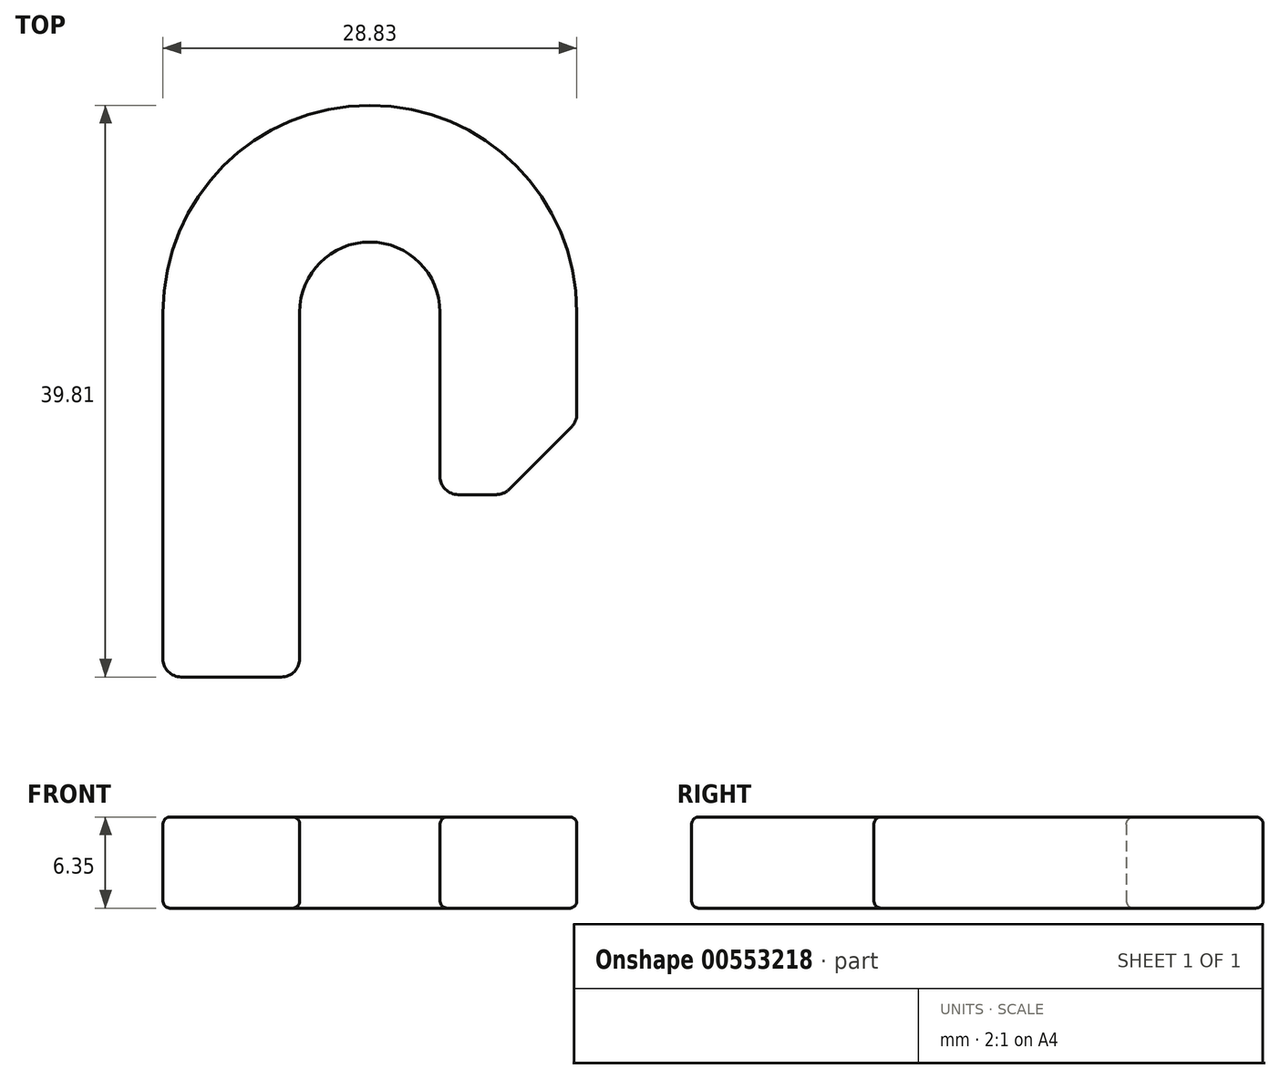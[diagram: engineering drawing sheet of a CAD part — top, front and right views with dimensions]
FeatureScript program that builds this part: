
annotation { "Feature Type Name" : "Feature", "Feature Type Description" : "" }
export const myFeature = defineFeature(function(context is Context, id is Id, definition is map)
    precondition{}
    {
        {
            var Q0;
            Q0=qCreatedBy(makeId("Top.planeOp"),FACE);
            var sketch = newSketch(context, id + "F0", { "sketchPlane" : qUnion([Q0])});
            skLineSegment(sketch, "E0", {"start": v(0, 0) * mm, "end": v(9.53, 0) * mm});
            skLineSegment(sketch, "E1", {"start": v(9.53, 0) * mm, "end": v(9.53, 25.4) * mm});
            skLineSegment(sketch, "E2", {"start": v(9.53, 25.4) * mm, "end": v(19.3, 25.4) * mm, "construction": true});
            skLineSegment(sketch, "E3", {"start": v(19.3, 25.4) * mm, "end": v(19.3, 0) * mm});
            skLineSegment(sketch, "E4", {"start": v(19.3, 0) * mm, "end": v(28.83, 0) * mm});
            skLineSegment(sketch, "E5", {"start": v(28.83, 0) * mm, "end": v(28.83, 25.4) * mm});
            skArc(sketch, "E6", {"start": v(19.3, 25.4) * mm, "mid": v(14.41, 30.29) * mm, "end": v(9.52, 25.4) * mm});
            skLineSegment(sketch, "E7", {"start": v(0, 0) * mm, "end": v(0, 25.4) * mm});
            skArc(sketch, "E8.trimOffspring", {"start": v(28.83, 25.4) * mm, "mid": v(14.41, 39.81) * mm, "end": v(0, 25.4) * mm});
            skLineSegment(sketch, "E9", {"start": v(19.3, 12.7) * mm, "end": v(28.83, 12.7) * mm});
            skSolve(sketch);
        }
        {
            var Q0;
            Q0=makeQuery(id+"F0.imprint","IMPRINT",FACE,{"disambiguationData":[TD([[makeQuery(id+"F0.imprint","IMPRINT",EDGE,{"derivedFrom":sQuery(id+"F0.wireOp",EDGE,"E0")}),1.0]])]});
            extrude(context, id + "F1", {"entities" : qUnion([Q0]), "depth" : 6.35 * mm, "offsetDistance" : 25.4 * mm});
        }
        {
            var Q0;
            Q0=makeQuery(id+"F1.opExtrude","SWEPT_EDGE",EDGE,{"disambiguationData":[OSD([sQuery(id+"F0.wireOp",EDGE,"E5"),sQuery(id+"F0.wireOp",EDGE,"E9")])]});
            chamfer(context, id + "F2", {"entities" : qUnion([Q0]), "width" : 5.08 * mm, "tangentPropagation" : true});
        }
        {
            var Q0;
            {var subQ0=sQuery(id+"F0.wireOp",EDGE,"E9");Q0=makeQuery(id+"F2.opChamfer","BLEND_EDGE",EDGE,{"blendedFrom":[makeQuery(id+"F1.opExtrude","SWEPT_EDGE",EDGE,{"disambiguationData":[OSD([sQuery(id+"F0.wireOp",EDGE,"E5"),subQ0])]}),makeQuery(id+"F1.opExtrude","SWEPT_FACE",FACE,{"disambiguationData":[OSD([subQ0])]})],"blendedInto":[makeQuery(id+"F1.opExtrude","SWEPT_FACE",FACE,{"disambiguationData":[OSD([subQ0])]})]});}
            var Q1;
            {var subQ0=sQuery(id+"F0.wireOp",EDGE,"E5");Q1=makeQuery(id+"F2.opChamfer","BLEND_EDGE",EDGE,{"blendedFrom":[makeQuery(id+"F1.opExtrude","SWEPT_EDGE",EDGE,{"disambiguationData":[OSD([subQ0,sQuery(id+"F0.wireOp",EDGE,"E9")])]}),makeQuery(id+"F1.opExtrude","SWEPT_FACE",FACE,{"disambiguationData":[OSD([subQ0])]})],"blendedInto":[makeQuery(id+"F1.opExtrude","SWEPT_FACE",FACE,{"disambiguationData":[OSD([subQ0])]})]});}
            var Q2;
            Q2=makeQuery(id+"F1.opExtrude","SWEPT_EDGE",EDGE,{"disambiguationData":[OSD([sQuery(id+"F0.wireOp",EDGE,"E3"),sQuery(id+"F0.wireOp",EDGE,"E9")])]});
            var Q3;
            Q3=makeQuery(id+"F1.opExtrude","SWEPT_EDGE",EDGE,{"disambiguationData":[OSD([sQuery(id+"F0.wireOp",EDGE,"E0"),sQuery(id+"F0.wireOp",EDGE,"E7")])]});
            var Q4;
            Q4=makeQuery(id+"F1.opExtrude","SWEPT_EDGE",EDGE,{"disambiguationData":[OSD([sQuery(id+"F0.wireOp",EDGE,"E0"),sQuery(id+"F0.wireOp",EDGE,"E1")])]});
            fillet(context, id + "F3", {"entities" : qUnion([Q0, Q1, Q2, Q3, Q4]), "radius" : 1.27 * mm, "tangentPropagation" : true, "allowEdgeOverflow" : false});
        }
        {
            var Q0;
            Q0=makeQuery(id+"F1.opExtrude","CAP_FACE",FACE,{"disambiguationData":[OSD([sQuery(id+"F0.wireOp",EDGE,"E0"),sQuery(id+"F0.wireOp",EDGE,"E1"),sQuery(id+"F0.wireOp",EDGE,"E3"),sQuery(id+"F0.wireOp",EDGE,"E5"),sQuery(id+"F0.wireOp",EDGE,"E6"),sQuery(id+"F0.wireOp",EDGE,"E7"),sQuery(id+"F0.wireOp",EDGE,"E8.trimOffspring"),sQuery(id+"F0.wireOp",EDGE,"E9")])],"isStart":false});
            var Q1;
            Q1=makeQuery(id+"F1.opExtrude","CAP_FACE",FACE,{"disambiguationData":[OSD([sQuery(id+"F0.wireOp",EDGE,"E0"),sQuery(id+"F0.wireOp",EDGE,"E1"),sQuery(id+"F0.wireOp",EDGE,"E3"),sQuery(id+"F0.wireOp",EDGE,"E5"),sQuery(id+"F0.wireOp",EDGE,"E6"),sQuery(id+"F0.wireOp",EDGE,"E7"),sQuery(id+"F0.wireOp",EDGE,"E8.trimOffspring"),sQuery(id+"F0.wireOp",EDGE,"E9")])],"isStart":true});
            fillet(context, id + "F4", {"entities" : qUnion([Q0, Q1]), "radius" : 0.5 * mm, "tangentPropagation" : true, "allowEdgeOverflow" : false});
        }
    });
